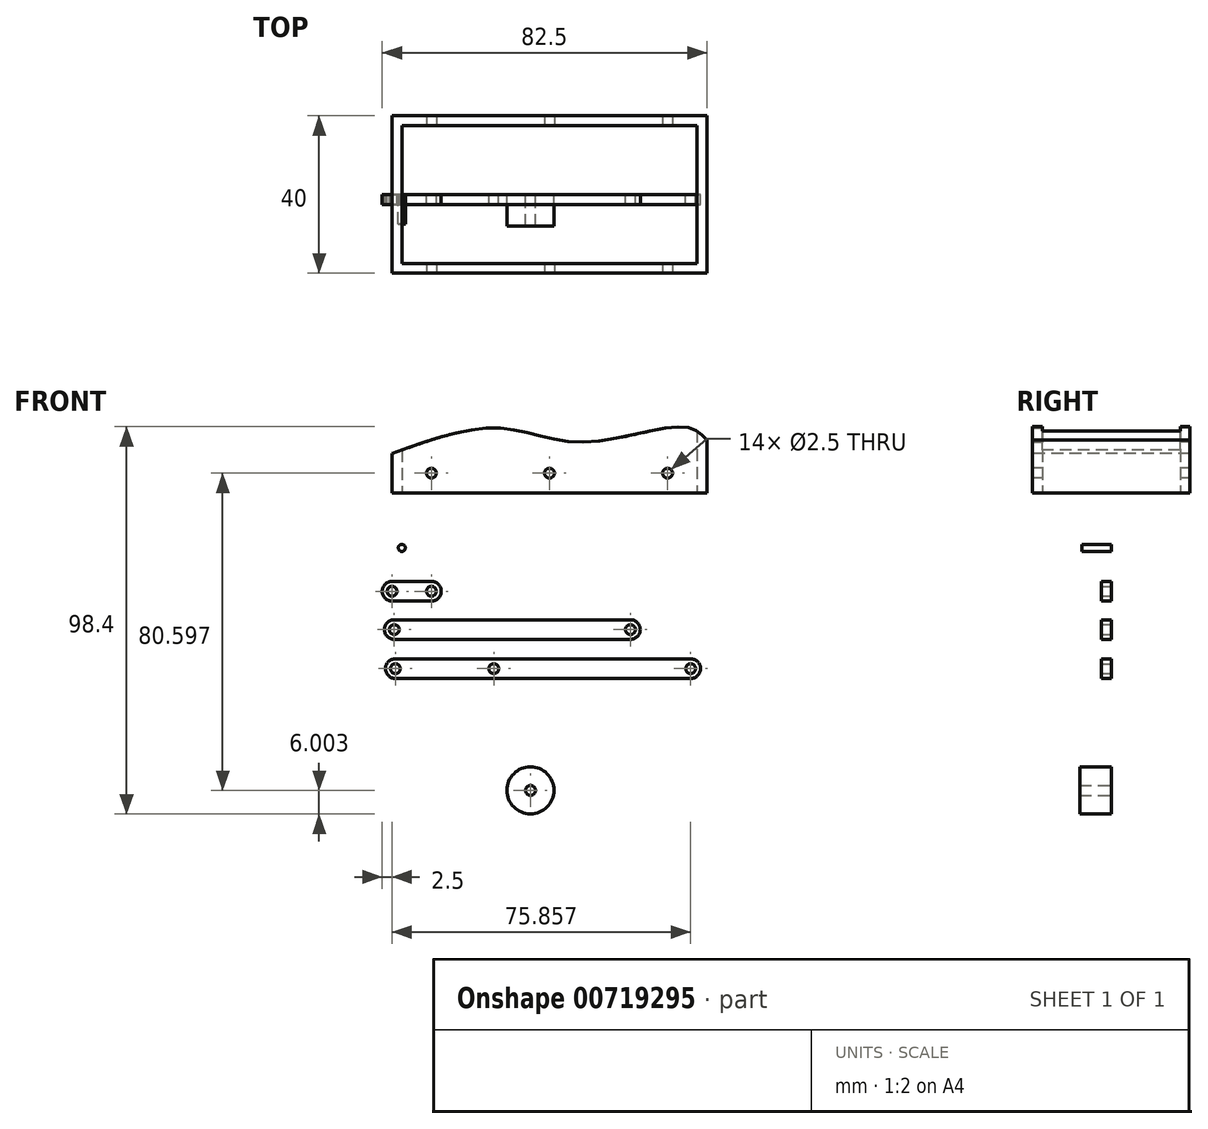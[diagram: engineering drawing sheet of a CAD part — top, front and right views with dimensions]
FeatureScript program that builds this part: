
annotation { "Feature Type Name" : "Feature", "Feature Type Description" : "" }
export const myFeature = defineFeature(function(context is Context, id is Id, definition is map)
    precondition{}
    {
        {
            assignVariable(context, id + "F0", {"name" : "thickness", "anyValue" : 2.5});
        }
        {
            var Q0;
            Q0=qCreatedBy(makeId("Front.planeOp"),FACE);
            var sketch = newSketch(context, id + "F1", { "sketchPlane" : qUnion([Q0])});
            skArc(sketch, "E0", {"start": v(0, 2.5) * mm, "mid": v(-2.5, 0) * mm, "end": v(0, -2.5) * mm});
            skArc(sketch, "E1", {"start": v(10, -2.5) * mm, "mid": v(12.5, 0) * mm, "end": v(10, 2.5) * mm});
            skLineSegment(sketch, "E2", {"start": v(0, 2.5) * mm, "end": v(10, 2.5) * mm});
            skLineSegment(sketch, "E3", {"start": v(0, -2.5) * mm, "end": v(10, -2.5) * mm});
            skCircle(sketch, "E4", {"center": v(0, 0) * mm, "radius": 1.25 * mm});
            skCircle(sketch, "E5", {"center": v(10, 0) * mm, "radius": 1.25 * mm});
            skSolve(sketch);
        }
        {
            var Q0;
            Q0=makeQuery(id+"F1.imprint","IMPRINT",FACE,{"disambiguationData":[TD([[makeQuery(id+"F1.imprint","IMPRINT",EDGE,{"derivedFrom":sQuery(id+"F1.wireOp",EDGE,"E0")}),1.0]])]});
            extrude(context, id + "F2", {"entities" : qUnion([Q0]), "depth" : (getVariable(context, 'thickness')) * mm, "offsetDistance" : 25 * mm});
        }
        {
            var Q0;
            Q0=qCreatedBy(makeId("Front.planeOp"),FACE);
            var sketch = newSketch(context, id + "F3", { "sketchPlane" : qUnion([Q0])});
            skArc(sketch, "E6", {"start": v(0.57, -7.23) * mm, "mid": v(-1.93, -9.73) * mm, "end": v(0.57, -12.23) * mm});
            skArc(sketch, "E7", {"start": v(60.57, -12.23) * mm, "mid": v(63.07, -9.73) * mm, "end": v(60.57, -7.23) * mm});
            skLineSegment(sketch, "E8", {"start": v(0.57, -7.23) * mm, "end": v(60.57, -7.23) * mm});
            skLineSegment(sketch, "E9", {"start": v(0.57, -12.23) * mm, "end": v(60.57, -12.23) * mm});
            skCircle(sketch, "E10", {"center": v(0.57, -9.73) * mm, "radius": 1.25 * mm});
            skCircle(sketch, "E11", {"center": v(60.57, -9.73) * mm, "radius": 1.25 * mm});
            skSolve(sketch);
        }
        {
            var Q0;
            Q0=makeQuery(id+"F3.imprint","IMPRINT",FACE,{"disambiguationData":[TD([[makeQuery(id+"F3.imprint","IMPRINT",EDGE,{"derivedFrom":sQuery(id+"F3.wireOp",EDGE,"E6")}),1.0]])]});
            extrude(context, id + "F4", {"entities" : qUnion([Q0]), "depth" : (getVariable(context, 'thickness')) * mm, "offsetDistance" : 25 * mm});
        }
        {
            var Q0;
            Q0=qCreatedBy(makeId("Front.planeOp"),FACE);
            var sketch = newSketch(context, id + "F5", { "sketchPlane" : qUnion([Q0])});
            skArc(sketch, "E12", {"start": v(0.86, -17.16) * mm, "mid": v(-1.64, -19.66) * mm, "end": v(0.86, -22.16) * mm});
            skArc(sketch, "E13", {"start": v(75.86, -22.16) * mm, "mid": v(78.36, -19.66) * mm, "end": v(75.86, -17.16) * mm});
            skLineSegment(sketch, "E14", {"start": v(0.86, -17.16) * mm, "end": v(75.86, -17.16) * mm});
            skLineSegment(sketch, "E15", {"start": v(0.86, -22.16) * mm, "end": v(75.86, -22.16) * mm});
            skCircle(sketch, "E16", {"center": v(0.86, -19.66) * mm, "radius": 1.25 * mm});
            skCircle(sketch, "E17", {"center": v(75.86, -19.66) * mm, "radius": 1.25 * mm});
            skCircle(sketch, "E18", {"center": v(25.86, -19.66) * mm, "radius": 1.25 * mm});
            skSolve(sketch);
        }
        {
            var Q0;
            Q0=makeQuery(id+"F5.imprint","IMPRINT",FACE,{"disambiguationData":[TD([[makeQuery(id+"F5.imprint","IMPRINT",EDGE,{"derivedFrom":sQuery(id+"F5.wireOp",EDGE,"E12")}),1.0]])]});
            extrude(context, id + "F6", {"entities" : qUnion([Q0]), "depth" : (getVariable(context, 'thickness')) * mm, "offsetDistance" : 25 * mm});
        }
        {
            var Q0;
            Q0=qCreatedBy(makeId("Top.planeOp"),FACE);
            cPlane(context, id + "F7", {"entities" : qUnion([Q0]), "cplaneType" : CPlaneType.OFFSET, "offset" : 25 * mm, "width" : 150 * mm, "height" : 150 * mm});
        }
        {
            var Q0;
            Q0=qCreatedBy(id+"F7.planeOp",FACE);
            var sketch = newSketch(context, id + "F8", { "sketchPlane" : qUnion([Q0])});
            skLineSegment(sketch, "E19.bottom", {"start": v(0, 20) * mm, "end": v(80, 20) * mm});
            skLineSegment(sketch, "E19.top", {"start": v(0, -20) * mm, "end": v(80, -20) * mm});
            skLineSegment(sketch, "E19.left", {"start": v(0, 20) * mm, "end": v(0, -20) * mm});
            skLineSegment(sketch, "E19.right", {"start": v(80, 20) * mm, "end": v(80, -20) * mm});
            skLineSegment(sketch, "E20.0", {"start": v(2.5, 17.5) * mm, "end": v(77.5, 17.5) * mm});
            skLineSegment(sketch, "E20.1", {"start": v(2.5, 17.5) * mm, "end": v(2.5, -17.5) * mm});
            skLineSegment(sketch, "E20.2", {"start": v(2.5, -17.5) * mm, "end": v(77.5, -17.5) * mm});
            skLineSegment(sketch, "E20.3", {"start": v(77.5, 17.5) * mm, "end": v(77.5, -17.5) * mm});
            skSolve(sketch);
        }
        {
            var Q0;
            Q0=makeQuery(id+"F8.imprint","IMPRINT",FACE,{"disambiguationData":[TD([[makeQuery(id+"F8.imprint","IMPRINT",EDGE,{"derivedFrom":sQuery(id+"F8.wireOp",EDGE,"E19.bottom")}),-1.0]])]});
            extrude(context, id + "F9", {"entities" : qUnion([Q0]), "depth" : 20 * mm, "offsetDistance" : 25 * mm});
        }
        {
            var Q0;
            Q0=makeQuery(id+"F9.opExtrude","SWEPT_FACE",FACE,{"disambiguationData":[OSD([sQuery(id+"F8.wireOp",EDGE,"E19.top")])]});
            var sketch = newSketch(context, id + "F10", { "sketchPlane" : qUnion([Q0])});
            skCircle(sketch, "E21", {"center": v(10, 30) * mm, "radius": 1.25 * mm});
            skCircle(sketch, "E22", {"center": v(70, 30) * mm, "radius": 1.25 * mm});
            skCircle(sketch, "E23", {"center": v(40, 30) * mm, "radius": 1.25 * mm});
            skPoint(sketch, "E23.centerSnap0", {"position": v(40, 25) * mm});
            skSolve(sketch);
        }
        {
            var Q0;
            Q0=qSketchRegion(id+"F10",true);
            extrude(context, id + "F11", {"entities" : qUnion([Q0]), "operationType" : NewBodyOperationType.REMOVE, "endBound" : BoundingType.THROUGH_ALL, "oppositeDirection" : true, "depth" : 25 * mm, "offsetDistance" : 25 * mm});
        }
        {
            var Q0;
            Q0=qCreatedBy(makeId("Front.planeOp"),FACE);
            var sketch = newSketch(context, id + "F12", { "sketchPlane" : qUnion([Q0])});
            skCircle(sketch, "E24", {"center": v(2.49, 11.02) * mm, "radius": 0.9 * mm});
            skSolve(sketch);
        }
        {
            var Q0;
            Q0=makeQuery(id+"F12.imprint","IMPRINT",FACE,{"disambiguationData":[TD([[makeQuery(id+"F12.imprint","IMPRINT",EDGE,{"derivedFrom":sQuery(id+"F12.wireOp",EDGE,"E24")}),1.0]])]});
            extrude(context, id + "F13", {"entities" : qUnion([Q0]), "depth" : (getVariable(context, 'thickness') * 3) * mm, "offsetDistance" : 25 * mm});
        }
        {
            var Q0;
            Q0=makeQuery(id+"F9.opExtrude","SWEPT_FACE",FACE,{"disambiguationData":[OSD([sQuery(id+"F8.wireOp",EDGE,"E19.top")])]});
            var sketch = newSketch(context, id + "F14", { "sketchPlane" : qUnion([Q0])});
            skFitSpline(sketch, "E25", {"points": [v(0, 35) * mm, v(27.2, 41.45) * mm, v(48.56, 37.9) * mm, v(74.59, 41.73) * mm, v(80, 38.37) * mm], "startDerivative": vector(95.15, 34.2) * mm, "endDerivative": vector(27.8, -31.81) * mm});
            skLineSegment(sketch, "E26", {"start": v(0, 35) * mm, "end": v(-10.13, 49.1) * mm});
            skLineSegment(sketch, "E27", {"start": v(-10.13, 49.1) * mm, "end": v(68.15, 61.14) * mm});
            skLineSegment(sketch, "E28", {"start": v(68.15, 61.14) * mm, "end": v(95.86, 42.57) * mm});
            skLineSegment(sketch, "E29", {"start": v(95.86, 42.57) * mm, "end": v(80, 38.37) * mm});
            skSolve(sketch);
        }
        {
            var Q0;
            Q0 = qSketchRegion(id + "F14", true);
            extrude(context, id + "F15", {"entities" : qUnion([Q0]), "operationType" : NewBodyOperationType.REMOVE, "endBound" : BoundingType.THROUGH_ALL, "oppositeDirection" : true, "depth" : 25 * mm, "offsetDistance" : 25 * mm});
        }
        {
            var Q0;
            Q0=qCreatedBy(makeId("Front.planeOp"),FACE);
            var sketch = newSketch(context, id + "F16", { "sketchPlane" : qUnion([Q0])});
            skCircle(sketch, "E30", {"center": v(35.18, -50.6) * mm, "radius": 1.25 * mm});
            skCircle(sketch, "E31", {"center": v(35.18, -50.6) * mm, "radius": 6 * mm});
            skSolve(sketch);
        }
        {
            var Q0;
            Q0=makeQuery(id+"F16.imprint","IMPRINT",FACE,{"disambiguationData":[TD([[makeQuery(id+"F16.imprint","IMPRINT",EDGE,{"derivedFrom":sQuery(id+"F16.wireOp",EDGE,"E30")}),-1.0]])]});
            extrude(context, id + "F17", {"entities" : qUnion([Q0]), "depth" : 8 * mm, "offsetDistance" : 25 * mm});
        }
    });
